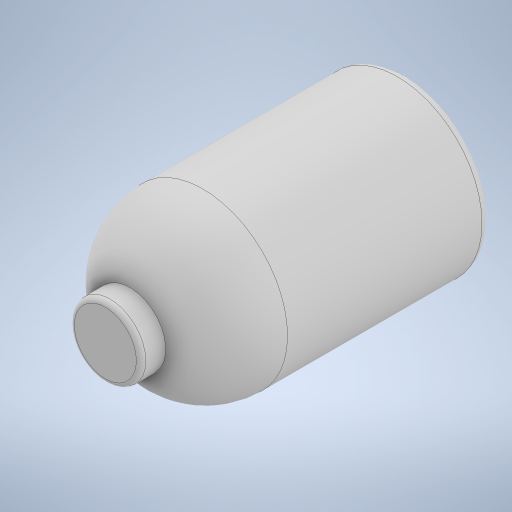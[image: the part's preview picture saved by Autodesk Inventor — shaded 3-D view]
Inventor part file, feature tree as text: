
AUTODESK INVENTOR PART (.ipt)
format: ipt  version: 2023 (Build 270158000, 158)  size: 247,808 bytes
history: native  units: in
note: dims shown in document units (in); Inventor stores cm internally (conversion verified against a paired STEP export)
features: fillet x3, extrude x2, sketch x2
ambient origin geometry x8: Origin, YZ Plane, XZ Plane, XY Plane, X Axis, Y Axis, Z Axis, Center Point
bodies: Solid1 (feature_tree)
feature tree (7):
  extrude  "Extrusion1"  Depth=1.1811in TaperAngle=0.0deg
  fillet  "Fillet1"  Radius=0.3287in
  extrude  "Extrusion2"  Depth=0.0394in TaperAngle=0.0deg
  fillet  "Fillet2"  Radius=0.0394in
  fillet  "Fillet3"  Radius=0.0197in
  sketch  "Sketch1"  dims[d0=0.7087in d1=1.1811in d2=0.0in d3=0.3287in]
  sketch  "Sketch2"  dims[d4=0.2992in d5=0.0787in d6=0.0394in d7=0.0in d8=0.0in d9=0.0394in d10=0.0197in]
